# Revit family: 162-MONOMANDO LAVAPLATOS VERSO
name_source: partatom
category: Aparatos sanitarios
units: mm (PartAtom-declared; Revit-internal decimal feet)

## family parameters
Compartido = No
Corte con vacíos al cargar = No
Cota de conector redondo = Radio de uso
Número OmniClass = 23.45.05.14.21.11
Punto de cálculo de habitación = No
Se basa en plano de trabajo = Sí
Siempre vertical = Sí
Tipo de pieza = Normal
Título OmniClass = Bath/Shower Units

## types (1)
- LAVAPLATOS EXTRAIBLE VERSO
    Bath Tub Material = <Por categoría>
    CWFU = 1
    Cold Water Radius = 8 mm
    Elevación por defecto = 121.92 cm
    F_Alto = 26.8 cm
    F_Ancho = 9 cm
    F_Color = Latón cromado
    F_Peso = 0.00 kgf
    F_Productos incluidos = Base auxiliar y flexibles de conexión a la red de agua
    F_Profundidad = 22.5 cm
    F_SKU = SGLP65403061CB
    F_Tipo de instalación = Vertical
    Faucet Material = <Por categoría>
    HWFU = 1
    Sanitary Radius = 20 mm
    URL = https://briggs.cl
    WFU = 2

## geometry (parser evidence)
native form markers: Sweep x3
no freeform markers — native parametric forms only
